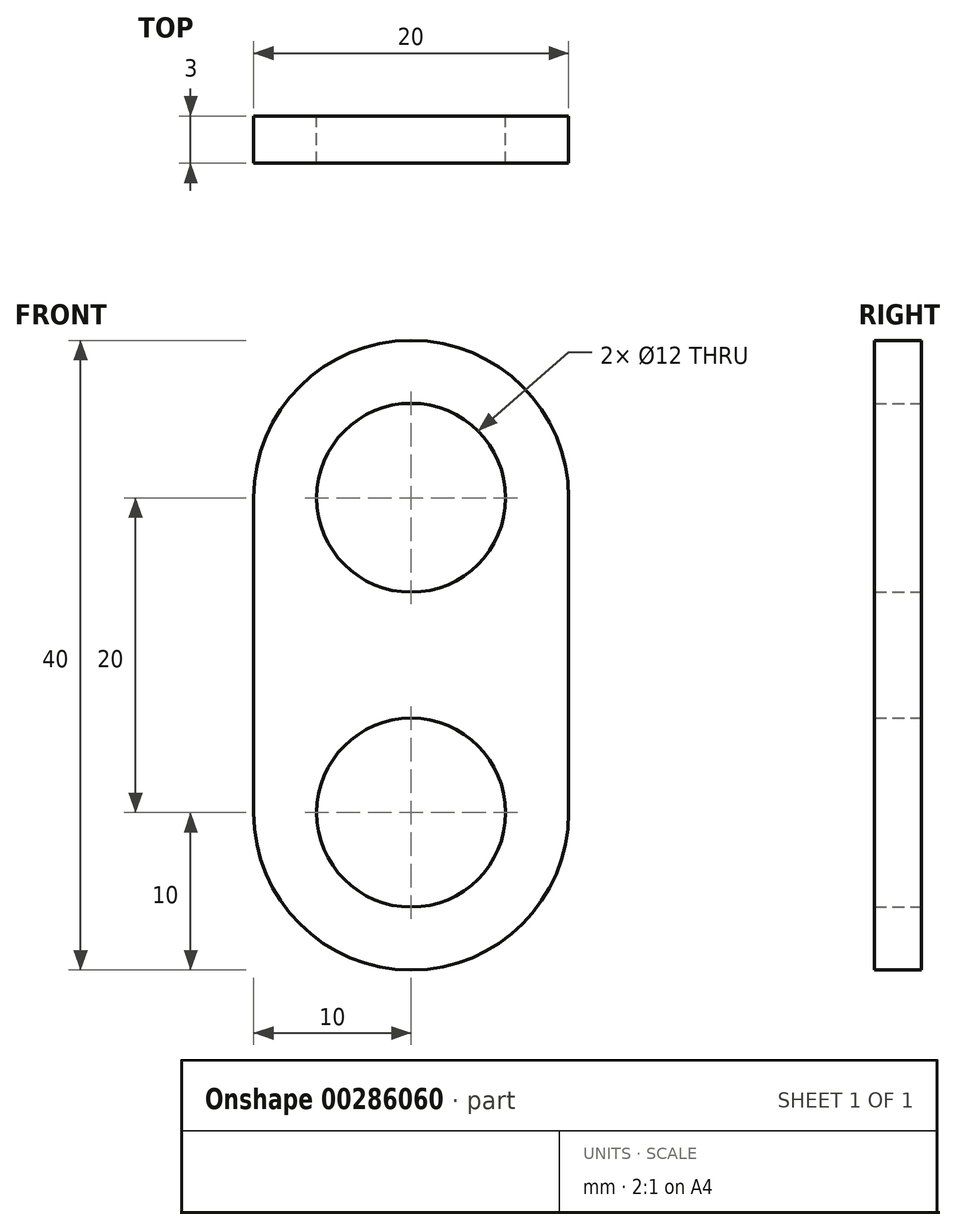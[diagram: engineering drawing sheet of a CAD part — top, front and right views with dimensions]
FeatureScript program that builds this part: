
annotation { "Feature Type Name" : "Feature", "Feature Type Description" : "" }
export const myFeature = defineFeature(function(context is Context, id is Id, definition is map)
    precondition{}
    {
        {
            var Q0;
            Q0=qCreatedBy(makeId("Front.planeOp"),FACE);
            var sketch = newSketch(context, id + "F0", { "sketchPlane" : qUnion([Q0])});
            skLineSegment(sketch, "E0.bottom", {"start": v(10, -10) * mm, "end": v(-10, -10) * mm, "construction": true});
            skLineSegment(sketch, "E0.top", {"start": v(10, 10) * mm, "end": v(-10, 10) * mm, "construction": true});
            skLineSegment(sketch, "E0.left", {"start": v(10, -10) * mm, "end": v(10, 10) * mm});
            skLineSegment(sketch, "E0.right", {"start": v(-10, -10) * mm, "end": v(-10, 10) * mm});
            skPoint(sketch, "E0.middle", {"position": v(0, 0) * mm});
            skArc(sketch, "E1", {"start": v(10, 10) * mm, "mid": v(0, 20) * mm, "end": v(-10, 10) * mm});
            skArc(sketch, "E2", {"start": v(-10, -10) * mm, "mid": v(0, -20) * mm, "end": v(10, -10) * mm});
            skCircle(sketch, "E3", {"center": v(0, -10) * mm, "radius": 6 * mm});
            skCircle(sketch, "E4", {"center": v(0, 10) * mm, "radius": 6 * mm});
            skSolve(sketch);
        }
        {
            var Q0;
            Q0=makeQuery(id+"F0.imprint","IMPRINT",FACE,{"disambiguationData":[TD([[makeQuery(id+"F0.imprint","IMPRINT",EDGE,{"derivedFrom":sQuery(id+"F0.wireOp",EDGE,"E0.left")}),1.0]])]});
            extrude(context, id + "F1", {"entities" : qUnion([Q0]), "depth" : 3 * mm});
        }
    });
